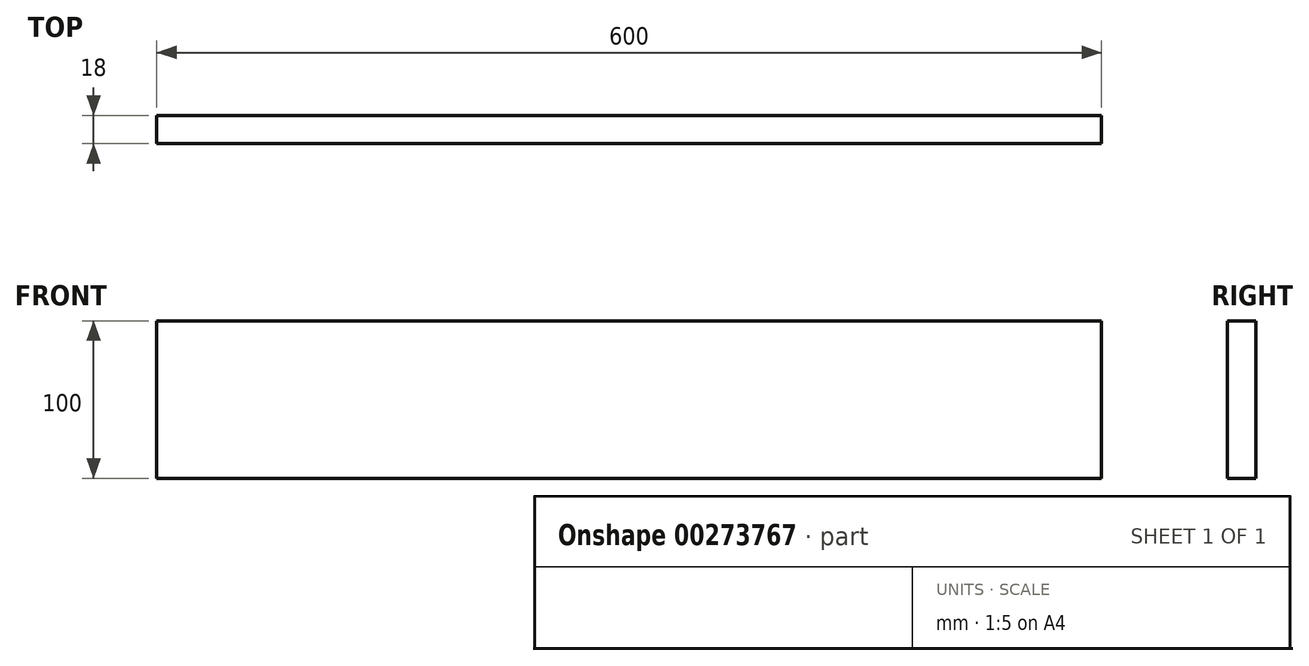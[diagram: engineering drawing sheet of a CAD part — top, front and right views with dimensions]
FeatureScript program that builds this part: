
annotation { "Feature Type Name" : "Feature", "Feature Type Description" : "" }
export const myFeature = defineFeature(function(context is Context, id is Id, definition is map)
    precondition{}
    {
        {
            var Q0;
            Q0=qCreatedBy(makeId("Front.planeOp"),FACE);
            var sketch = newSketch(context, id + "F0", { "sketchPlane" : qUnion([Q0])});
            skLineSegment(sketch, "E0.bottom", {"start": v(-300, -50) * mm, "end": v(300, -50) * mm});
            skLineSegment(sketch, "E0.top", {"start": v(-300, 50) * mm, "end": v(300, 50) * mm});
            skLineSegment(sketch, "E0.left", {"start": v(-300, -50) * mm, "end": v(-300, 50) * mm});
            skLineSegment(sketch, "E0.right", {"start": v(300, -50) * mm, "end": v(300, 50) * mm});
            skPoint(sketch, "E0.middle", {"position": v(0, 0) * mm});
            skSolve(sketch);
        }
        {
            var Q0;
            Q0=makeQuery(id+"F0.imprint","IMPRINT",FACE,{"disambiguationData":[TD([[makeQuery(id+"F0.imprint","IMPRINT",EDGE,{"derivedFrom":sQuery(id+"F0.wireOp",EDGE,"E0.bottom")}),1.0]])]});
            extrude(context, id + "F1", {"entities" : qUnion([Q0]), "depth" : 18 * mm});
        }
    });
